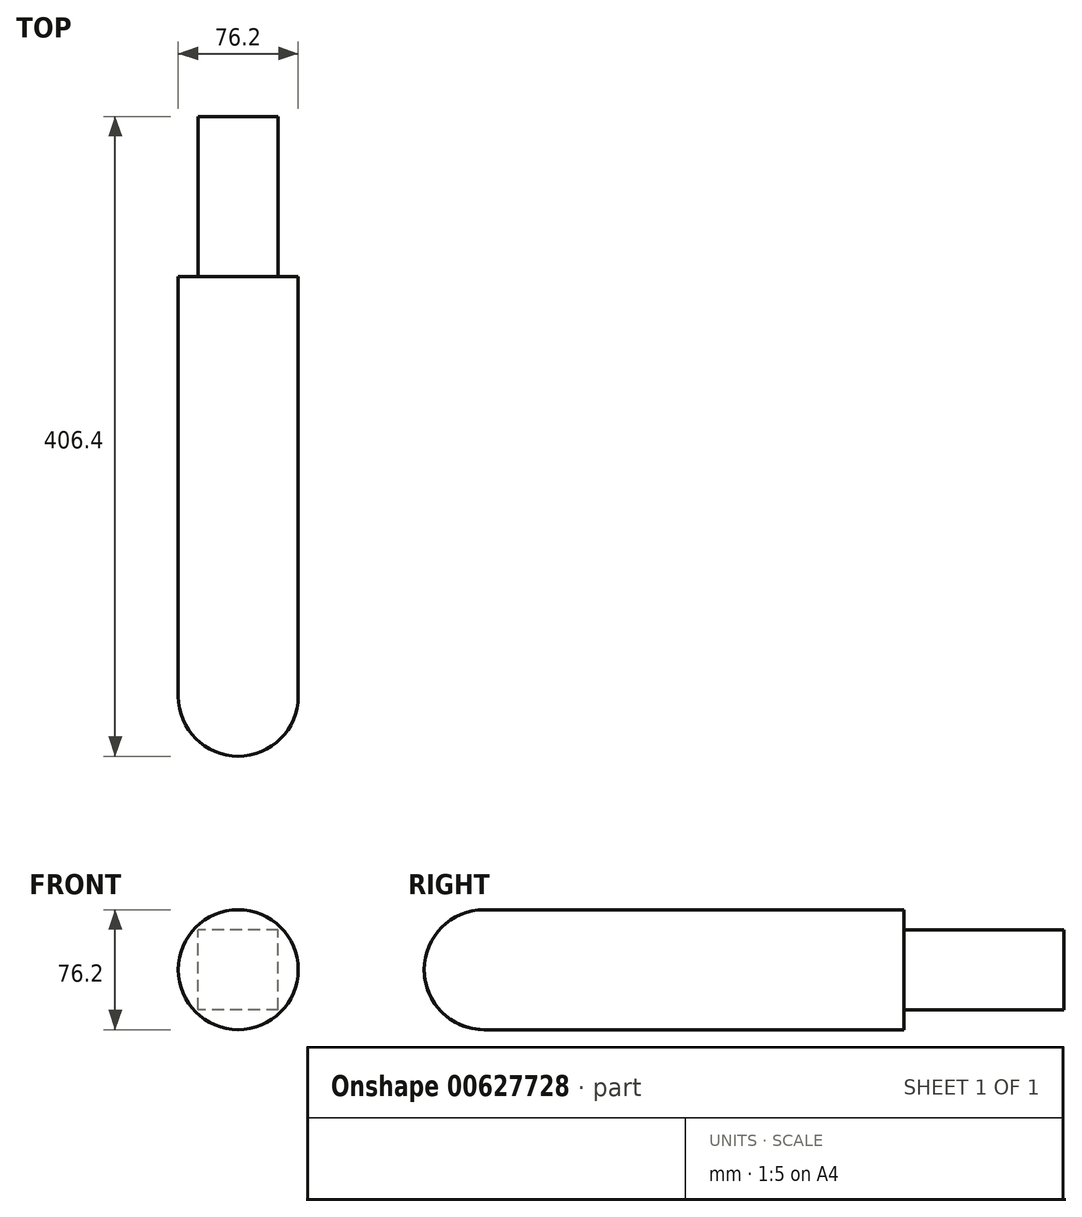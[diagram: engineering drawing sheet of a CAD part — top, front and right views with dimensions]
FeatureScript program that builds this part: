
annotation { "Feature Type Name" : "Feature", "Feature Type Description" : "" }
export const myFeature = defineFeature(function(context is Context, id is Id, definition is map)
    precondition{}
    {
        {
            var Q0;
            Q0=qCreatedBy(makeId("Front.planeOp"),FACE);
            var sketch = newSketch(context, id + "F0", { "sketchPlane" : qUnion([Q0])});
            skLineSegment(sketch, "E0.bottom", {"start": v(25.4, -25.4) * mm, "end": v(-25.4, -25.4) * mm});
            skLineSegment(sketch, "E0.top", {"start": v(25.4, 25.4) * mm, "end": v(-25.4, 25.4) * mm});
            skLineSegment(sketch, "E0.left", {"start": v(25.4, -25.4) * mm, "end": v(25.4, 25.4) * mm});
            skLineSegment(sketch, "E0.right", {"start": v(-25.4, -25.4) * mm, "end": v(-25.4, 25.4) * mm});
            skPoint(sketch, "E0.middle", {"position": v(0, 0) * mm});
            skSolve(sketch);
        }
        {
            var Q0;
            Q0=makeQuery(id+"F0.imprint","IMPRINT",FACE,{"disambiguationData":[TD([[makeQuery(id+"F0.imprint","IMPRINT",EDGE,{"derivedFrom":sQuery(id+"F0.wireOp",EDGE,"E0.bottom")}),-1.0]])]});
            extrude(context, id + "F1", {"entities" : qUnion([Q0]), "depth" : 101.6 * mm, "offsetDistance" : 25.4 * mm});
        }
        {
            var Q0;
            Q0=makeQuery(id+"F1.opExtrude","CAP_FACE",FACE,{"disambiguationData":[OSD([sQuery(id+"F0.wireOp",EDGE,"E0.bottom"),sQuery(id+"F0.wireOp",EDGE,"E0.top"),sQuery(id+"F0.wireOp",EDGE,"E0.left"),sQuery(id+"F0.wireOp",EDGE,"E0.right")])],"isStart":false});
            var sketch = newSketch(context, id + "F2", { "sketchPlane" : qUnion([Q0])});
            skCircle(sketch, "E1", {"center": v(0, 0) * mm, "radius": 38.1 * mm});
            skSolve(sketch);
        }
        {
            var Q0;
            Q0=makeQuery(id+"F2.imprint","IMPRINT",FACE,{"disambiguationData":[TD([[makeQuery(id+"F2.imprint","IMPRINT",EDGE,{"derivedFrom":makeQuery(id+"F1.opExtrude","CAP_EDGE",EDGE,{"disambiguationData":[OSD([sQuery(id+"F0.wireOp",EDGE,"E0.bottom")])],"isStart":false})}),-1.0]])]});
            var Q1;
            Q1=makeQuery(id+"F2.imprint","IMPRINT",FACE,{"disambiguationData":[TD([[makeQuery(id+"F2.imprint","IMPRINT",EDGE,{"derivedFrom":sQuery(id+"F2.wireOp",EDGE,"E1")}),1.0]])]});
            extrude(context, id + "F3", {"entities" : qUnion([Q0, Q1]), "operationType" : NewBodyOperationType.ADD, "depth" : 304.8 * mm, "offsetDistance" : 25.4 * mm});
        }
        {
            var Q0;
            Q0=makeQuery(id+"F3.opExtrude","CAP_EDGE",EDGE,{"disambiguationData":[OSD([sQuery(id+"F2.wireOp",EDGE,"E1")])],"isStart":false});
            fillet(context, id + "F4", {"entities" : qUnion([Q0]), "radius" : 38.1 * mm, "tangentPropagation" : true, "allowEdgeOverflow" : false});
        }
    });
